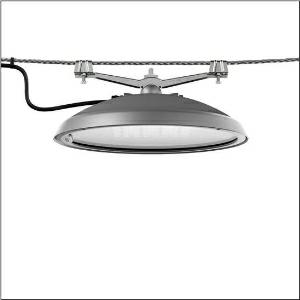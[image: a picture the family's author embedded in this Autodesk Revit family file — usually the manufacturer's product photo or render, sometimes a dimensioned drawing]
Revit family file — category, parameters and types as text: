
# Revit family: dl_r__50_iq_mini___p1_0s_5xa248u31f08ge_4109
name_source: partatom
category: Lighting Fixtures
units: mm (PartAtom-declared; Revit-internal decimal feet)

## family parameters
Cut with Voids When Loaded = No
Host = Face
Light Source = No
Part Type = Normal
Room Calculation Point = No
Round Connector Dimension = Use Diameter
Shared = No

## types (1)
- --- (1 x LED, 5030 lm, 32.7 W, 3000K)
    Apparent Load = 33 VA
    CIE Flux Codes = 23 54 93 100 100
    Color Rendering = 70
    Color Temperature = 3000K
    Default Elevation = 1800 mm
    Description = DL® 50 iQ mini, catenary luminaire, primary light control with lens, of PMMA, primary optical cover: cover, of toughened safety glass, transparent, light distribution: P1.0s, light emission: direct distribution, primary light characteristic: symmetric, installation type: suspended mounting, LED, High Power LED, rated luminous flux: 5.030lm, luminous efficacy: 154lm/W, light colour: 730, colour temperature: 3000K, control gear: iQ Street-Remote, control: optimised constant luminous flux control (CLO 2.0), Desk-Remote (wireless, voltage-free reading and setting of iQ features in the workshop via application-optimized NFC function/RFID function), Light-Fading, Smart-Wire, Night-Set, Lumen-Switch, Temp-Guard, Auto-Match, Street-Remote, mains connection: 230..240V, AC, 50/60Hz, start of lifetime: 33W, end of service life: 34W, reduction: 16W, luminaire housing, of diecast aluminium, powder-coated, Siteco® metallic grey (DB 702S), diameter: 500mm, height: 115mm, mounting height: 4..12m, protection rating (complete): IP66, insulation class (complete): insulation class II (safety insulation), certification: CE, ENEC, ENEC+, VDE, impact resistance: IK08, permissible operating ambient temperature for outdoor applications: -25..+40°C, standard-compliant lighting for roads and squares, packaging unit: 1 piece

Light Distribution: P1.0s
    Height = 124 mm  [stored 0.406824 ft]
    Lamp = 1 x LED
    Lamp Light Flux = 5030 lm
    Lamp Power = 32.7 W
    Lamp count = 1
    Length = 500 mm
    Luminous efficacy = 154 lm/W
    Manufacturer = Siteco
    ModVariant = No
    Model = 5XA248U31F08GE
    Number of Poles = 1
    OnlyDefault = Yes
    Power Factor = 1
    Product Name = DL® 50 iQ mini | P1.0s
    Product group = catenary luminaire
    ProductGroupID = 6300
    Protection Class = Protection class II
    Protection Degree = IP 66
    RLX_Detail_Level = 1
    RLX_Emergency_Light_Flux = 0 lm
    RLX_Emergency_Type = 0
    RLX_Emergency_Type_DB = No
    RlxData = <blob elided: 123769 chars, md5=7bccdb30>
    Socket = socket
    Standby Power = 0 W
    System Light Flux = 5030 lm
    System Power = 33 W
    Type Comments = factory setting: luminous flux: 100 % | dim-lin: 254 | 340 mA
    Type Image = l_1242791.jpg
    URL = http://relux.com
    VarID = @adj_140222
    Voltage = 0 V
    Weight = 0.00 kg
    Width = 0 mm  [stored 0 ft]

note: [stored X ft] marks values corroborated as IEEE doubles in the binary element streams (Revit-internal decimal feet)

## geometry (parser evidence)
native form markers: Blend x4, Sweep x13
no freeform markers — native parametric forms only
